# Revit family: Hekatron_Raumlufttechnik_LRZ Basis_DE_22.01
name_source: partatom
category: Brandmelder
revit_build: Autodesk Revit 2018 (Build: 20190510_1515(x64)
units: mm (PartAtom-declared; Revit-internal decimal feet)

## family parameters
Basisbauteil = Fläche
Beim Laden mit Abzugskörper schneiden = Nein
Bemaßung runder Anschluss = Durchmesser verwenden
Beschriftungsausrichtung beibehalten = Ja
Gemeinsam genutzt = Nein
OmniClass-Nummer = 23.85.30.21
OmniClass-Titel = Environmental Detection/Registration
Raumberechnungspunkt = Nein
Teiletyp = Normal

## types (1)
- LRZ Base
    Bauartgenehmigungen = Z-78.6-177
    Beschreibung = Die Lüftungs-Rauchschalter-Zentrale Basis (LRZ Basis) ist Netzgerät, Handtaster, Resettaster, Alarmspeicher und Betriebszustandsanzeige in einem Gerät. Geeignet zur Steuerung von Brand- und Rauchschutzklappen und zur Abschaltung von Lüftungsanlagen in unterschiedlichen Anwendungsfeldern von Industrie- bis Verwaltungsgebäuden.
    Betriebsspannung = 230 V AC
    Breite (mm) = 60.5
    Farbe = weiß, ähnlich RAL 9003
    Hersteller = Hekatron
    Höhe (mm) = 146.0
    Kabeleinführung = oben, unten, hinten
    Link zu Ausschreibungstext = https://www.meinhplus.de
    Link zu Produktinformation = https://www.hekatron-planungstools.de
    Link zu ausschreiben.de = http://www.ausschreiben.de
    Link zum Datenblatt = https://www.hekatron-planungstools.de
    Material = PC-ABS
    Modell = LRZ Basis
    Montageart = Aufputz
    Schutzart = IP 30
    Tiefe (mm) = 146.0
    Typenkommentare = Lüftungs Rauchschalter Zentrale Basis
    UB A&S Artikel Nummer = 31-5400005-01-01
    URL = https://www.hekatron-brandschutz.de
    Version des BIM Objektes = 22.01
    Vorgabe-Ansicht = 1200 mm
    Zulässige Umgebungstemperatur = -10 °C bis +50 °C

## geometry (parser evidence)
native form markers: Extrusion x1, Sweep x2
no freeform markers — native parametric forms only
